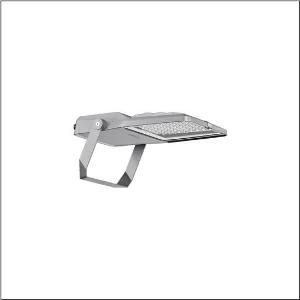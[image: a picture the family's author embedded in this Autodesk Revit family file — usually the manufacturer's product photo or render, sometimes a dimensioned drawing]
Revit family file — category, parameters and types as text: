
# Revit family: floodlight_fl_21_iq_mini___pl43_5xa7771d2a1a_9b6a
name_source: partatom
category: Lighting Fixtures
units: mm (PartAtom-declared; Revit-internal decimal feet)

## family parameters
Cut with Voids When Loaded = No
Host = Face
Light Source = No
Part Type = Normal
Room Calculation Point = No
Round Connector Dimension = Use Diameter
Shared = No

## types (1)
- --- (1 x LED, 18290 lm, 143 W, 3000K)
    Apparent Load = 143 VA
    CIE Flux Codes = 27 78 99 100 100
    Color Rendering = 70
    Color Temperature = 3000K
    Default Elevation = 1800 mm
    Description = Floodlight FL 21 iQ mini, floodlight, primary light control with lens, of PMMA, primary optical cover: protective disc, of toughened safety glass, transparent, light distribution: PL43, light emission: direct distribution, installation type: surface-mounted, LED, High Power LED, rated luminous flux: 18.290lm, luminous efficacy: 128lm/W, light colour: 730, colour temperature: 3000K, control: Auto-Match, Temp-Guard, Lumen-Switch, Night-Set, Smart-Wire, Light-Fading, Desk-Remote (wireless, voltage-free reading and setting of iQ features in the workshop via application-optimized NFC function/RFID function), optimised constant luminous flux control (CLO 2.0), with terminal, 6-pole, mains connection: 220..240V, AC, 50/60Hz, start of lifetime: 143W, end of service life: 152W, reduction: 61W, luminaire housing, of diecast aluminium, powder-coated, Siteco® metallic grey (DB 702S), corrosivity category C5 mid according to DIN EN ISO 12944, sealing non-destructively replaceable, mounting bracket, of steel, galvanised, powder-coated, Siteco® metallic grey (DB 702S), protection rating (complete): IP66, insulation class (complete): insulation class II (safety insulation), certification: CE, ENEC, VDE, protection symbol: D, impact resistance: IK08, permissible operating ambient temperature: -40..+40°C, permissible operating ambient temperature for outdoor applications: -40..+50°C, standard: DIN EN 12944, LABS conformity tested according to VDMA 24364:2018-05, packaging unit: 1 piece

Light Distribution: PL43
    Height = 70 mm
    Lamp = 1 x LED
    Lamp Light Flux = 18290 lm
    Lamp Power = 143 W
    Lamp count = 1
    Length = 485 mm
    Luminous efficacy = 128 lm/W
    Manufacturer = Siteco
    ModVariant = No
    Model = 5XA7771D2A1A
    Number of Poles = 1
    OnlyDefault = Yes
    Power Factor = 1
    Product Name = Floodlight FL 21 iQ mini | PL43
    Product group = floodlight | pylon annexe
    ProductGroupID = 6200
    Protection Class = Protection class II
    Protection Degree = IP 66
    RLX_Detail_Level = 1
    RLX_Emergency_Light_Flux = 0 lm
    RLX_Emergency_Type = 0
    RLX_Emergency_Type_DB = No
    RlxData = <blob elided: 96309 chars, md5=9edb31ab>
    Socket = socket
    Standby Power = 0 W
    System Light Flux = 18290 lm
    System Power = 143 W
    Type Comments = factory setting: luminous flux: 100 % | dim-lin: 254 | 730 mA
    Type Image = l_1006845.jpg
    URL = http://relux.com
    VarID = @adj_112239
    Voltage = 0 V
    Weight = 0.00 kg
    Width = 337 mm

## geometry (parser evidence)
native form markers: Blend x4, Sweep x12
no freeform markers — native parametric forms only
